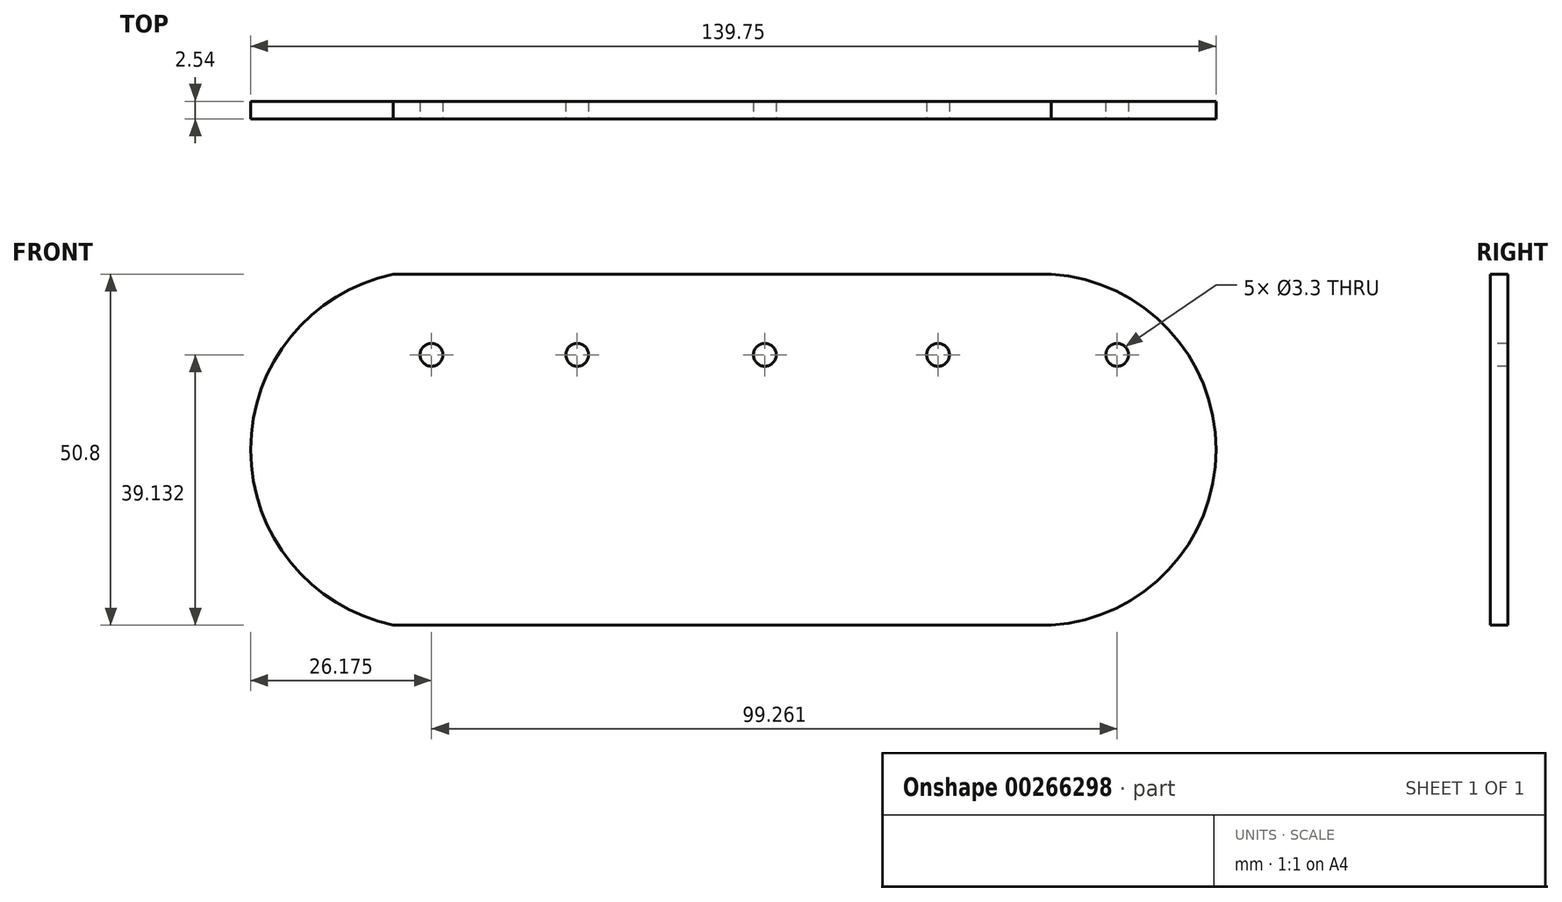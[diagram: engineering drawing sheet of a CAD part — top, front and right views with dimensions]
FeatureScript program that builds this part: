
annotation { "Feature Type Name" : "Feature", "Feature Type Description" : "" }
export const myFeature = defineFeature(function(context is Context, id is Id, definition is map)
    precondition{}
    {
        {
            var Q0;
            Q0=qCreatedBy(makeId("Front.planeOp"),FACE);
            var sketch = newSketch(context, id + "F0", { "sketchPlane" : qUnion([Q0])});
            skLineSegment(sketch, "E0", {"start": v(0, 0) * mm, "end": v(76.2, 0) * mm});
            skLineSegment(sketch, "E1", {"start": v(76.2, 50.8) * mm, "end": v(0, 50.8) * mm});
            skLineSegment(sketch, "E2", {"start": v(0, 50.8) * mm, "end": v(-19.05, 50.8) * mm});
            skArc(sketch, "E3", {"start": v(76.2, 0) * mm, "mid": v(100.04, 25.4) * mm, "end": v(76.2, 50.8) * mm});
            skArc(sketch, "E4", {"start": v(-38.1, 50.8) * mm, "mid": v(-39.67, 50.85) * mm, "end": v(-41.24, 50.8) * mm});
            skArc(sketch, "E5", {"start": v(-19.05, 50.8) * mm, "mid": v(-39.7, 25.4) * mm, "end": v(-19.05, 0) * mm});
            skPoint(sketch, "E5.endSnap0", {"position": v(-19.05, 50.8) * mm});
            skPoint(sketch, "E6.trimOffspring.end.orphan", {"position": v(-76.2, 50.8) * mm});
            skLineSegment(sketch, "E7.trimOffspring", {"start": v(-19.05, 0) * mm, "end": v(0, 0) * mm});
            skPoint(sketch, "E8.start.orphan", {"position": v(-55.5, 0) * mm});
            skPoint(sketch, "E9.orphan", {"position": v(-27.75, 0) * mm});
            skPoint(sketch, "E10.start.orphan", {"position": v(152.4, 0) * mm});
            skPoint(sketch, "E11.orphan", {"position": v(152.4, 50.8) * mm});
            skSolve(sketch);
        }
        {
            var Q0;
            {var subQ6=sQuery(id+"F0.wireOp",EDGE,"E3");Q0=makeQuery(id+"F0.imprint","IMPRINT",FACE,{"disambiguationData":[TD([[makeQuery(id+"F0.imprint","IMPRINT",EDGE,{"derivedFrom":subQ6}),1.0]])]});}
            extrude(context, id + "F1", {"entities" : qUnion([Q0]), "depth" : 2.54 * mm});
        }
        {
            var Q0;
            Q0=makeQuery(id+"F1.opExtrude","CAP_FACE",FACE,{"disambiguationData":[OSD([sQuery(id+"F0.wireOp",EDGE,"E0"),sQuery(id+"F0.wireOp",EDGE,"E10"),sQuery(id+"F0.wireOp",EDGE,"E1"),sQuery(id+"F0.wireOp",EDGE,"lx8ZJy22-e0qu-SJEc-MJLZ-UQqIdSeRy6Xp")])],"isStart":false});
            var sketch = newSketch(context, id + "F2", { "sketchPlane" : qUnion([Q0])});
            skCircle(sketch, "E12", {"center": v(59.8, 39.13) * mm, "radius": 1.65 * mm});
            skCircle(sketch, "E13", {"center": v(85.73, 39.13) * mm, "radius": 1.65 * mm});
            skCircle(sketch, "E14", {"center": v(34.72, 39.13) * mm, "radius": 1.65 * mm});
            skCircle(sketch, "E15", {"center": v(7.57, 39.13) * mm, "radius": 1.65 * mm});
            skCircle(sketch, "E16", {"center": v(-13.53, 39.13) * mm, "radius": 1.65 * mm});
            skSolve(sketch);
        }
        {
            var Q0;
            Q0=makeQuery(id+"F2.imprint","IMPRINT",FACE,{"disambiguationData":[TD([[makeQuery(id+"F2.imprint","IMPRINT",EDGE,{"derivedFrom":sQuery(id+"F2.wireOp",EDGE,"E12")}),1.0]])]});
            var Q1;
            Q1=makeQuery(id+"F2.imprint","IMPRINT",FACE,{"disambiguationData":[TD([[makeQuery(id+"F2.imprint","IMPRINT",EDGE,{"derivedFrom":sQuery(id+"F2.wireOp",EDGE,"E13")}),1.0]])]});
            var Q2;
            Q2=makeQuery(id+"F2.imprint","IMPRINT",FACE,{"disambiguationData":[TD([[makeQuery(id+"F2.imprint","IMPRINT",EDGE,{"derivedFrom":sQuery(id+"F2.wireOp",EDGE,"E14")}),1.0]])]});
            var Q3;
            Q3=makeQuery(id+"F2.imprint","IMPRINT",FACE,{"disambiguationData":[TD([[makeQuery(id+"F2.imprint","IMPRINT",EDGE,{"derivedFrom":sQuery(id+"F2.wireOp",EDGE,"E15")}),1.0]])]});
            var Q4;
            Q4=makeQuery(id+"F2.imprint","IMPRINT",FACE,{"disambiguationData":[TD([[makeQuery(id+"F2.imprint","IMPRINT",EDGE,{"derivedFrom":sQuery(id+"F2.wireOp",EDGE,"E16")}),1.0]])]});
            extrude(context, id + "F3", {"entities" : qUnion([Q0, Q1, Q2, Q3, Q4]), "operationType" : NewBodyOperationType.REMOVE, "oppositeDirection" : true, "depth" : 25.4 * mm});
        }
    });
